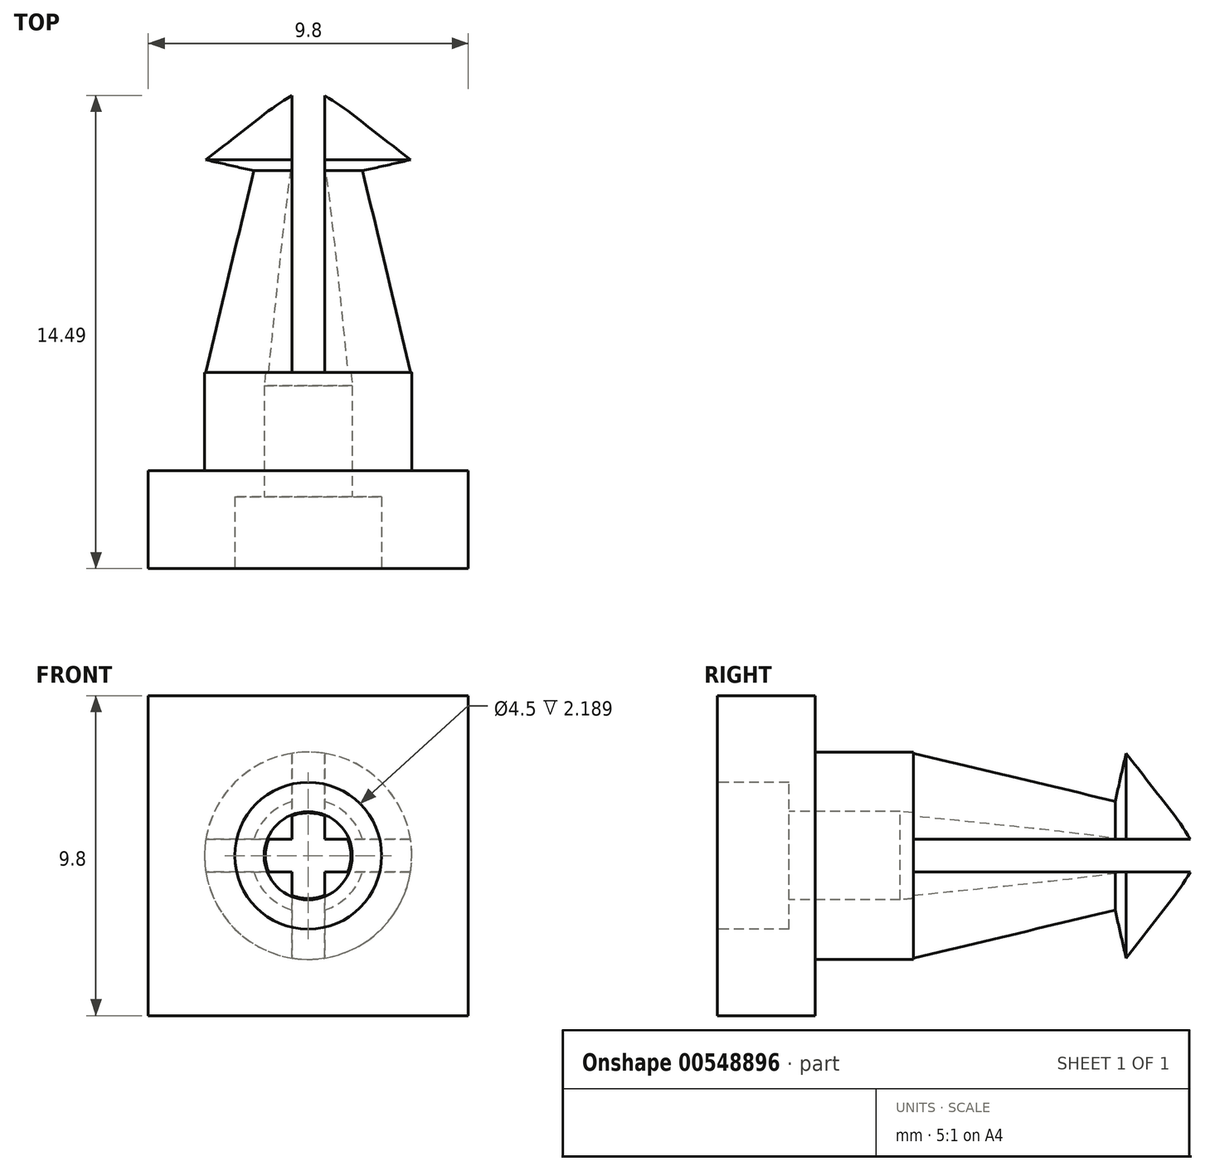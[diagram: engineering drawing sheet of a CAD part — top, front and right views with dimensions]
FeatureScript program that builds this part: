
annotation { "Feature Type Name" : "Feature", "Feature Type Description" : "" }
export const myFeature = defineFeature(function(context is Context, id is Id, definition is map)
    precondition{}
    {
        {
            var Q0;
            Q0=qCreatedBy(makeId("Front.planeOp"),FACE);
            var sketch = newSketch(context, id + "F0", { "sketchPlane" : qUnion([Q0])});
            skLineSegment(sketch, "E0.bottom", {"start": v(-4.9, 4.9) * mm, "end": v(4.9, 4.9) * mm});
            skLineSegment(sketch, "E0.top", {"start": v(-4.9, -4.9) * mm, "end": v(4.9, -4.9) * mm});
            skLineSegment(sketch, "E0.left", {"start": v(-4.9, 4.9) * mm, "end": v(-4.9, -4.9) * mm});
            skLineSegment(sketch, "E0.right", {"start": v(4.9, 4.9) * mm, "end": v(4.9, -4.9) * mm});
            skPoint(sketch, "E0.middle", {"position": v(0, 0) * mm});
            skCircle(sketch, "E1", {"center": v(0, 0) * mm, "radius": 2.75 * mm});
            skCircle(sketch, "E2", {"center": v(0, 0) * mm, "radius": 1.35 * mm});
            skSolve(sketch);
        }
        {
            var Q0;
            Q0=qCreatedBy(makeId("Right.planeOp"),FACE);
            var sketch = newSketch(context, id + "F1", { "sketchPlane" : qUnion([Q0])});
            skPoint(sketch, "E3.middle", {"position": v(0, 0) * mm});
            skLineSegment(sketch, "E4.right", {"start": v(-1.5, 3.18) * mm, "end": v(-1.5, 2.25) * mm});
            skLineSegment(sketch, "E5", {"start": v(4.1, 1.35) * mm, "end": v(13.15, 0.5) * mm});
            skLineSegment(sketch, "E6", {"start": v(10.68, 1.74) * mm, "end": v(11.02, 3.18) * mm});
            skLineSegment(sketch, "E7", {"start": v(10.68, 1.74) * mm, "end": v(4.5, 3.18) * mm});
            skLineSegment(sketch, "E8", {"start": v(11.02, 3.18) * mm, "end": v(13.15, 0.5) * mm});
            skLineSegment(sketch, "E9.top", {"start": v(0.69, 2.25) * mm, "end": v(-1.5, 2.25) * mm});
            skLineSegment(sketch, "E9.left", {"start": v(0.69, 1.35) * mm, "end": v(0.69, 2.25) * mm});
            skLineSegment(sketch, "E10.bottom", {"start": v(4.1, 0) * mm, "end": v(14.6, 0) * mm});
            skLineSegment(sketch, "E10.right", {"start": v(14.6, 0) * mm, "end": v(14.6, 0.26) * mm});
            skLineSegment(sketch, "E11", {"start": v(4.1, 0.25) * mm, "end": v(4.1, 0) * mm});
            skLineSegment(sketch, "E12.trimOffspring", {"start": v(4.1, 0) * mm, "end": v(18.85, 0) * mm});
            skLineSegment(sketch, "E13", {"start": v(0.69, 1.35) * mm, "end": v(4.1, 1.35) * mm});
            skLineSegment(sketch, "E14", {"start": v(-1.5, 3.18) * mm, "end": v(4.5, 3.18) * mm});
            skSolve(sketch);
        }
        {
            var Q0;
            Q0=makeQuery(id+"F1.imprint","IMPRINT",FACE,{"disambiguationData":[TD([[makeQuery(id+"F1.imprint","IMPRINT",EDGE,{"derivedFrom":sQuery(id+"F1.wireOp",EDGE,"E4.bottom")}),1.0]])]});
            var Q1;
            {var subQ0=sQuery(id+"F1.wireOp",EDGE,"pFF8Vxng-QkmA-qD3w-jG2V-iSrp1qWLh6pe.right");Q1=makeQuery(id+"F1.imprint","IMPRINT",FACE,{"disambiguationData":[TD([[makeQuery(id+"F1.imprint","IMPRINT",EDGE,{"derivedFrom":subQ0}),1.0]])]});}
            var Q2;
            {var subQ0=sQuery(id+"F1.wireOp",EDGE,"E8");Q2=makeQuery(id+"F1.imprint","IMPRINT",FACE,{"disambiguationData":[TD([[makeQuery(id+"F1.imprint","IMPRINT",EDGE,{"derivedFrom":subQ0}),-1.0]])]});}
            var Q3;
            {var subQ1=sQuery(id+"F1.wireOp",EDGE,"E6");var subQ4=sQuery(id+"F1.wireOp",EDGE,"E5");var subQ5=makeQuery(id+"F1.imprint","INTERSECT",VERTEX,{"derivedFrom":[subQ4,subQ1]});Q3=makeQuery(id+"F1.imprint","IMPRINT",FACE,{"disambiguationData":[TD([[makeQuery(id+"F1.imprint","IMPRINT",EDGE,{"disambiguationData":[TD([[subQ5,-1.0]])],"derivedFrom":subQ4}),1.0]])]});}
            var Q4;
            {var subQ5=sQuery(id+"F1.wireOp",EDGE,"E7");Q4=makeQuery(id+"F1.imprint","IMPRINT",FACE,{"disambiguationData":[TD([[makeQuery(id+"F1.imprint","IMPRINT",EDGE,{"derivedFrom":subQ5}),1.0]])]});}
            var Q5;
            Q5=sQuery(id+"F1.wireOp",EDGE,"E12.trimOffspring");
            revolve(context, id + "F2", {"entities" : qUnion([Q0, Q1, Q2, Q3, Q4]), "axis" : qUnion([Q5]), "revolveType" : RevolveType.FULL});
        }
        {
            var Q0;
            Q0=makeQuery(id+"F0.imprint","IMPRINT",FACE,{"disambiguationData":[TD([[makeQuery(id+"F0.imprint","IMPRINT",EDGE,{"derivedFrom":sQuery(id+"F0.wireOp",EDGE,"E0.bottom")}),-1.0]])]});
            extrude(context, id + "F3", {"entities" : qUnion([Q0]), "operationType" : NewBodyOperationType.ADD, "endBound" : BoundingType.SYMMETRIC, "depth" : 3 * mm, "offsetDistance" : 25 * mm});
        }
        {
            var Q0;
            Q0=qCreatedBy(makeId("Front.planeOp"),FACE);
            var sketch = newSketch(context, id + "F4", { "sketchPlane" : qUnion([Q0])});
            skLineSegment(sketch, "E15.bottom", {"start": v(-0.5, 5) * mm, "end": v(0.5, 5) * mm});
            skLineSegment(sketch, "E15.top", {"start": v(-0.5, -5) * mm, "end": v(0.5, -5) * mm});
            skLineSegment(sketch, "E15.left", {"start": v(-0.5, 5) * mm, "end": v(-0.5, -5) * mm});
            skLineSegment(sketch, "E15.right", {"start": v(0.5, 5) * mm, "end": v(0.5, -5) * mm});
            skPoint(sketch, "E15.middle", {"position": v(0, 0) * mm});
            skLineSegment(sketch, "E16.bottom", {"start": v(5, -0.5) * mm, "end": v(-5, -0.5) * mm});
            skLineSegment(sketch, "E16.top", {"start": v(5, 0.5) * mm, "end": v(-5, 0.5) * mm});
            skLineSegment(sketch, "E16.left", {"start": v(5, -0.5) * mm, "end": v(5, 0.5) * mm});
            skLineSegment(sketch, "E16.right", {"start": v(-5, -0.5) * mm, "end": v(-5, 0.5) * mm});
            skSolve(sketch);
        }
        {
            var Q0;
            Q0 = qSketchRegion(id + "F4", true);
            extrude(context, id + "F5", {"entities" : qUnion([Q0]), "operationType" : NewBodyOperationType.REMOVE, "oppositeDirection" : true, "depth" : 25 * mm, "offsetDistance" : 25 * mm, "hasSecondDirection" : true, "secondDirectionOppositeDirection" : true, "secondDirectionDepth" : 4.5 * mm});
        }
    });
